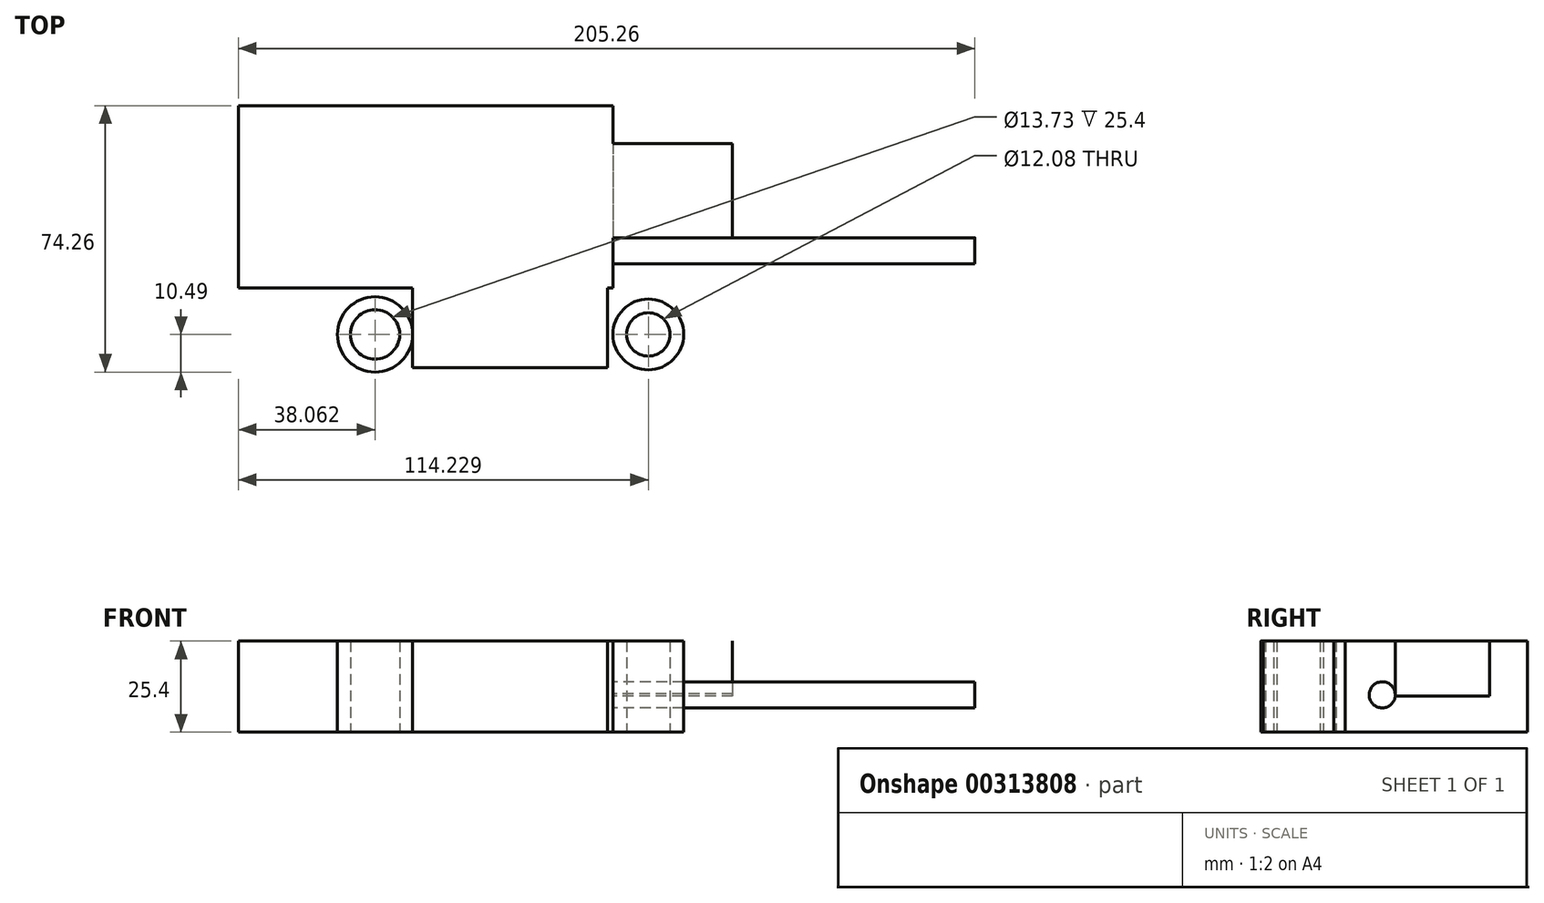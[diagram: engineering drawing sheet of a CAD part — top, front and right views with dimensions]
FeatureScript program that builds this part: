
annotation { "Feature Type Name" : "Feature", "Feature Type Description" : "" }
export const myFeature = defineFeature(function(context is Context, id is Id, definition is map)
    precondition{}
    {
        {
            var Q0;
            Q0=qCreatedBy(makeId("Top.planeOp"),FACE);
            var sketch = newSketch(context, id + "F0", { "sketchPlane" : qUnion([Q0])});
            skLineSegment(sketch, "E0.bottom", {"start": v(-35.43, 12.97) * mm, "end": v(18.84, 12.97) * mm});
            skLineSegment(sketch, "E0.top", {"start": v(-35.43, -9.26) * mm, "end": v(18.84, -9.26) * mm});
            skLineSegment(sketch, "E0.left", {"start": v(-35.43, 12.97) * mm, "end": v(-35.43, -9.26) * mm});
            skLineSegment(sketch, "E0.right", {"start": v(18.84, 12.97) * mm, "end": v(18.84, -9.26) * mm});
            skCircle(sketch, "E1", {"center": v(-45.92, 0) * mm, "radius": 10.49 * mm});
            skCircle(sketch, "E2", {"center": v(30.25, 0) * mm, "radius": 9.86 * mm});
            skCircle(sketch, "E3", {"center": v(-45.92, 0) * mm, "radius": 6.87 * mm});
            skCircle(sketch, "E4", {"center": v(30.25, 0) * mm, "radius": 6.04 * mm});
            skSolve(sketch);
        }
        {
            var Q0;
            {var subQ3=sQuery(id+"F0.wireOp",EDGE,"E0.bottom");Q0=makeQuery(id+"F0.imprint","IMPRINT",FACE,{"disambiguationData":[TD([[makeQuery(id+"F0.imprint","IMPRINT",EDGE,{"derivedFrom":subQ3}),-1.0]])]});}
            var Q1;
            Q1=makeQuery(id+"F0.imprint","IMPRINT",FACE,{"disambiguationData":[TD([[makeQuery(id+"F0.imprint","IMPRINT",EDGE,{"derivedFrom":sQuery(id+"F0.wireOp",EDGE,"E2")}),1.0]])]});
            var Q2;
            Q2=makeQuery(id+"F0.imprint","IMPRINT",FACE,{"disambiguationData":[TD([[makeQuery(id+"F0.imprint","IMPRINT",EDGE,{"derivedFrom":sQuery(id+"F0.wireOp",EDGE,"E1")}),1.0]])]});
            extrude(context, id + "F1", {"entities" : qUnion([Q0, Q1, Q2]), "depth" : 25.4 * mm});
        }
        {
            var Q0;
            Q0=makeQuery(id+"F1.opExtrude","SWEPT_FACE",FACE,{"disambiguationData":[OSD([sQuery(id+"F0.wireOp",EDGE,"E0.bottom")])]});
            var sketch = newSketch(context, id + "F2", { "sketchPlane" : qUnion([Q0])});
            skLineSegment(sketch, "E5.bottom", {"start": v(33.18, 0) * mm, "end": v(4.96, 0) * mm});
            skLineSegment(sketch, "E5.top", {"start": v(33.18, 25.4) * mm, "end": v(4.96, 25.4) * mm});
            skLineSegment(sketch, "E5.left", {"start": v(33.18, 0) * mm, "end": v(33.18, 25.4) * mm});
            skLineSegment(sketch, "E5.right", {"start": v(4.96, 0) * mm, "end": v(4.96, 25.4) * mm});
            skSolve(sketch);
        }
        {
            var Q0;
            Q0=makeQuery(id+"F2.imprint","IMPRINT",FACE,{"disambiguationData":[TD([[makeQuery(id+"F2.imprint","IMPRINT",EDGE,{"derivedFrom":sQuery(id+"F2.wireOp",EDGE,"E5.bottom")}),-1.0]])]});
            extrude(context, id + "F3", {"entities" : qUnion([Q0]), "operationType" : NewBodyOperationType.ADD, "depth" : 25.4 * mm});
        }
        {
            var Q0;
            Q0=makeQuery(id+"F3.opExtrude","SWEPT_FACE",FACE,{"disambiguationData":[OSD([sQuery(id+"F2.wireOp",EDGE,"E5.right")])]});
            extrude(context, id + "F4", {"entities" : qUnion([Q0]), "operationType" : NewBodyOperationType.ADD, "depth" : 25.4 * mm});
        }
        {
            var Q0;
            Q0=makeQuery(id+"F4.opExtrude","CAP_FACE",FACE,{"disambiguationData":[OSD([sQuery(id+"F2.wireOp",EDGE,"E5.right")])],"isStart":false});
            var sketch = newSketch(context, id + "F5", { "sketchPlane" : qUnion([Q0])});
            skCircle(sketch, "E6", {"center": v(23.34, 10.4) * mm, "radius": 3.64 * mm});
            skSolve(sketch);
        }
        {
            var Q0;
            Q0 = qSketchRegion(id + "F5", true);
            extrude(context, id + "F6", {"entities" : qUnion([Q0]), "operationType" : NewBodyOperationType.ADD, "depth" : 100.84 * mm});
        }
        {
            var Q0;
            Q0=makeQuery(id+"F3.opExtrude","SWEPT_FACE",FACE,{"disambiguationData":[OSD([sQuery(id+"F2.wireOp",EDGE,"E5.left")])]});
            var sketch = newSketch(context, id + "F7", { "sketchPlane" : qUnion([Q0])});
            skSolve(sketch);
        }
        {
            var Q0;
            {var subQ0=sQuery(id+"F2.wireOp",EDGE,"E5.left");Q0=makeQuery(id+"F7.imprint","IMPRINT",FACE,{"disambiguationData":[TD([[makeQuery(id+"F7.imprint","IMPRINT",EDGE,{"derivedFrom":makeQuery(id+"F3.opExtrude","CAP_EDGE",EDGE,{"disambiguationData":[OSD([subQ0])],"isStart":false})}),-1.0]])]});}
            extrude(context, id + "F8", {"entities" : qUnion([Q0]), "operationType" : NewBodyOperationType.ADD, "depth" : 25.4 * mm});
        }
        {
            var Q0;
            Q0=makeQuery(id+"F8.opExtrude","CAP_FACE",FACE,{"disambiguationData":[OSD([sQuery(id+"F0.wireOp",EDGE,"E0.bottom"),sQuery(id+"F2.wireOp",EDGE,"E5.bottom"),sQuery(id+"F2.wireOp",EDGE,"E5.top"),sQuery(id+"F2.wireOp",EDGE,"E5.left")])],"isStart":false});
            extrude(context, id + "F9", {"entities" : qUnion([Q0]), "operationType" : NewBodyOperationType.ADD, "depth" : 25.4 * mm});
        }
        {
            var Q0;
            {var subQ0=sQuery(id+"F2.wireOp",EDGE,"E5.left");var subQ1=makeQuery(id+"F7.imprint","IMPRINT",EDGE,{"derivedFrom":makeQuery(id+"F3.opExtrude","CAP_EDGE",EDGE,{"disambiguationData":[OSD([subQ0])],"isStart":false})});var subQ2=sQuery(id+"F2.wireOp",EDGE,"E5.right");Q0=makeQuery(id+"F9.boolean.opBoolean","MERGE",FACE,{"derivedFrom":[makeQuery(id+"F8.boolean.opBoolean","MERGE",FACE,{"derivedFrom":[makeQuery(id+"F4.boolean.opBoolean","MERGE",FACE,{"derivedFrom":[makeQuery(id+"F3.opExtrude","CAP_FACE",FACE,{"disambiguationData":[OSD([sQuery(id+"F2.wireOp",EDGE,"E5.bottom"),sQuery(id+"F2.wireOp",EDGE,"E5.top"),subQ0,subQ2])],"isStart":false}),makeQuery(id+"F4.opExtrude","SWEPT_FACE",FACE,{"disambiguationData":[OSD([subQ2]),TDD([makeQuery(id+"F3.opExtrude","CAP_EDGE",EDGE,{"disambiguationData":[OSD([subQ2])],"isStart":false})])]})]}),makeQuery(id+"F8.opExtrude","SWEPT_FACE",FACE,{"disambiguationData":[OSD([subQ0]),TDD([subQ1])]})]}),makeQuery(id+"F9.opExtrude","SWEPT_FACE",FACE,{"disambiguationData":[OSD([subQ0]),TDD([makeQuery(id+"F8.opExtrude","CAP_EDGE",EDGE,{"disambiguationData":[OSD([subQ0]),TDD([subQ1])],"isStart":false})])]})]});}
            var sketch = newSketch(context, id + "F10", { "sketchPlane" : qUnion([Q0])});
            skSolve(sketch);
        }
        {
            var Q0;
            {var subQ0=sQuery(id+"F2.wireOp",EDGE,"E5.right");Q0=makeQuery(id+"F10.imprint","IMPRINT",FACE,{"disambiguationData":[TD([[makeQuery(id+"F10.imprint","IMPRINT",EDGE,{"derivedFrom":makeQuery(id+"F4.opExtrude","CAP_EDGE",EDGE,{"disambiguationData":[OSD([subQ0]),TDD([makeQuery(id+"F3.opExtrude","CAP_EDGE",EDGE,{"disambiguationData":[OSD([subQ0])],"isStart":false})])],"isStart":false})}),-1.0]])]});}
            extrude(context, id + "F11", {"entities" : qUnion([Q0]), "operationType" : NewBodyOperationType.ADD, "depth" : 25.4 * mm});
        }
        {
            var Q0;
            {var subQ0=sQuery(id+"F2.wireOp",EDGE,"E5.right");Q0=makeQuery(id+"F11.boolean.opBoolean","MERGE",FACE,{"derivedFrom":[makeQuery(id+"F4.opExtrude","CAP_FACE",FACE,{"disambiguationData":[OSD([subQ0])],"isStart":false}),makeQuery(id+"F11.opExtrude","SWEPT_FACE",FACE,{"disambiguationData":[OSD([subQ0])]})]});}
            var sketch = newSketch(context, id + "F12", { "sketchPlane" : qUnion([Q0])});
            skLineSegment(sketch, "E7.bottom", {"start": v(53.24, 25.4) * mm, "end": v(26.96, 25.4) * mm});
            skLineSegment(sketch, "E7.top", {"start": v(53.24, 10.07) * mm, "end": v(26.96, 10.07) * mm});
            skLineSegment(sketch, "E7.left", {"start": v(53.24, 25.4) * mm, "end": v(53.24, 10.07) * mm});
            skLineSegment(sketch, "E7.right", {"start": v(26.96, 25.4) * mm, "end": v(26.96, 10.07) * mm});
            skSolve(sketch);
        }
        {
            var Q0;
            {var subQ1=sQuery(id+"F12.wireOp",EDGE,"E7.bottom");Q0=makeQuery(id+"F12.imprint","IMPRINT",FACE,{"disambiguationData":[TD([[makeQuery(id+"F12.imprint","IMPRINT",EDGE,{"derivedFrom":subQ1}),1.0]])]});}
            extrude(context, id + "F13", {"entities" : qUnion([Q0]), "operationType" : NewBodyOperationType.ADD, "depth" : 33.27 * mm});
        }
    });
